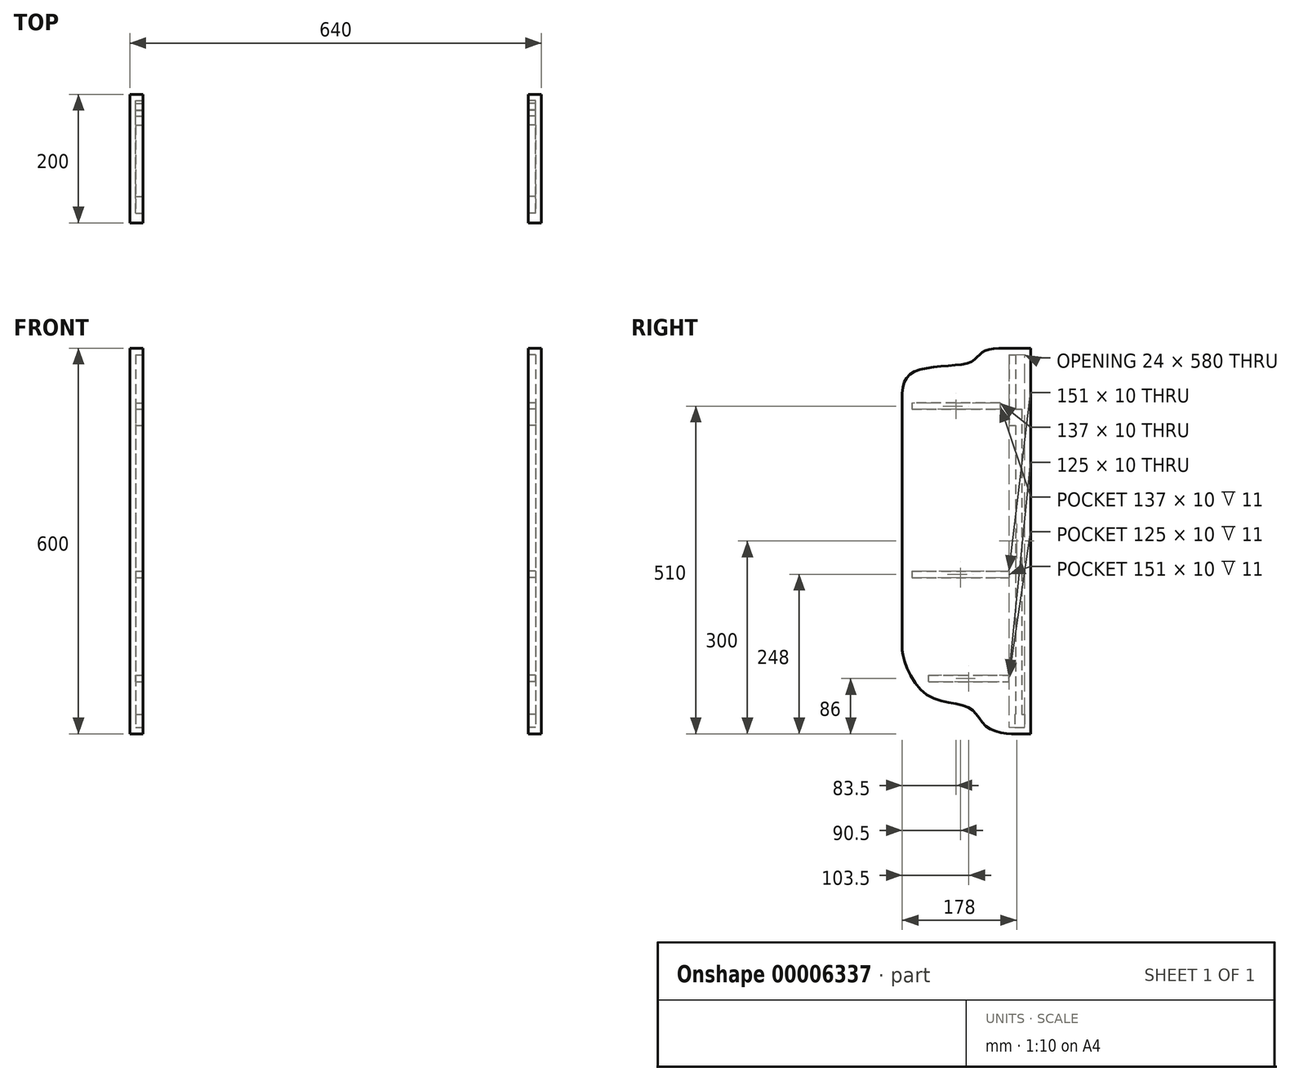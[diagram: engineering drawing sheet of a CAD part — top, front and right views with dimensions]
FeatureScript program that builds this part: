
annotation { "Feature Type Name" : "Feature", "Feature Type Description" : "" }
export const myFeature = defineFeature(function(context is Context, id is Id, definition is map)
    precondition{}
    {
        {
            var Q0;
            Q0=qCreatedBy(makeId("Right.planeOp"),FACE);
            var sketch = newSketch(context, id + "F0", { "sketchPlane" : qUnion([Q0])});
            skFitSpline(sketch, "E0.1.MirrorCS", {"points": [v(-200, 130) * mm, v(-165, 63) * mm, v(-95, 40) * mm, v(-70, 12) * mm, v(-30, 0) * mm], "startDerivative": vector(0, -133.97) * mm, "endDerivative": vector(166.38, 0) * mm});
            skLineSegment(sketch, "E0.4.MirrorCS", {"start": v(-200, 530) * mm, "end": v(-200, 117) * mm});
            skLineSegment(sketch, "E0.5.MirrorCS", {"start": v(0, 0) * mm, "end": v(0, 600) * mm});
            skLineSegment(sketch, "E1", {"start": v(-30, 0) * mm, "end": v(0, 0) * mm});
            skLineSegment(sketch, "E2.7", {"start": v(-40, 600) * mm, "end": v(0, 600) * mm});
            skFitSpline(sketch, "E3", {"points": [v(-1.8, 598.78) * mm, v(-75, 594) * mm, v(-95, 578) * mm, v(-180, 564) * mm, v(-198.07, 512.13) * mm], "startDerivative": vector(-411.19, 17.95) * mm, "endDerivative": vector(63.67, -327.47) * mm});
            skSolve(sketch);
        }
        {
            var Q0;
            Q0 = qSketchRegion(id + "F0", true);
            extrude(context, id + "F1", {"entities" : qUnion([Q0]), "oppositeDirection" : true, "depth" : 20 * mm});
        }
        {
            var Q0;
            Q0=qCreatedBy(makeId("Right.planeOp"),FACE);
            var sketch = newSketch(context, id + "F2", { "sketchPlane" : qUnion([Q0])});
            skLineSegment(sketch, "E4.13", {"start": v(-14, 495) * mm, "end": v(0, 495) * mm});
            skLineSegment(sketch, "E4.11", {"start": v(-20, 520) * mm, "end": v(0, 520) * mm});
            skLineSegment(sketch, "E4.14", {"start": v(-14, 505) * mm, "end": v(-14, 495) * mm});
            skLineSegment(sketch, "E4.16", {"start": v(-24, 505) * mm, "end": v(-24, 455) * mm});
            skLineSegment(sketch, "E4.10", {"start": v(-20, 520) * mm, "end": v(-20, 570) * mm});
            skLineSegment(sketch, "E4.17", {"start": v(-38, 455) * mm, "end": v(-24, 455) * mm});
            skLineSegment(sketch, "E4.9", {"start": v(-20, 570) * mm, "end": v(0, 570) * mm});
            skLineSegment(sketch, "E4.1", {"start": v(-38, 593.5) * mm, "end": v(-38, 455) * mm});
            skLineSegment(sketch, "E4.15", {"start": v(-14, 505) * mm, "end": v(-24, 505) * mm});
            skLineSegment(sketch, "E5", {"start": v(-36.5, 593.5) * mm, "end": v(-36.5, 594.5) * mm});
            skLineSegment(sketch, "E6", {"start": v(-32.5, 598.5) * mm, "end": v(-29.5, 598.5) * mm});
            skLineSegment(sketch, "E7", {"start": v(-38, 593.5) * mm, "end": v(-36.5, 593.5) * mm});
            skLineSegment(sketch, "E4.6", {"start": v(-29.5, 598.5) * mm, "end": v(-29.5, 600) * mm});
            skLineSegment(sketch, "E8.0", {"start": v(-29.5, 600) * mm, "end": v(0, 600) * mm});
            skPoint(sketch, "E9.orphan", {"position": v(-40, 600) * mm});
            skLineSegment(sketch, "E10.0", {"start": v(0, 495) * mm, "end": v(0, 520) * mm});
            skLineSegment(sketch, "E11.trimOffspring", {"start": v(0, 570) * mm, "end": v(0, 600) * mm});
            skPoint(sketch, "E12.orphan", {"position": v(0, 0) * mm});
            skLineSegment(sketch, "E13", {"start": v(-24, 463.64) * mm, "end": v(-24, 11.38) * mm, "construction": true});
            skLineSegment(sketch, "E14.bottom", {"start": v(0, 40) * mm, "end": v(-14, 40) * mm});
            skLineSegment(sketch, "E14.top", {"start": v(0, 0) * mm, "end": v(-30, 0) * mm});
            skLineSegment(sketch, "E14.left", {"start": v(0, 40) * mm, "end": v(0, 0) * mm});
            skLineSegment(sketch, "E14.right", {"start": v(-30, 40) * mm, "end": v(-30, 0) * mm});
            skLineSegment(sketch, "E15.top", {"start": v(-24, 30) * mm, "end": v(-14, 30) * mm});
            skLineSegment(sketch, "E15.left", {"start": v(-24, 40) * mm, "end": v(-24, 30) * mm});
            skLineSegment(sketch, "E15.right", {"start": v(-14, 40) * mm, "end": v(-14, 30) * mm});
            skLineSegment(sketch, "E16.trimOffspring", {"start": v(-24, 40) * mm, "end": v(-30, 40) * mm});
            skLineSegment(sketch, "E17.bottom", {"start": v(-190, 502) * mm, "end": v(-38, 502) * mm});
            skLineSegment(sketch, "E17.top", {"start": v(-190, 518) * mm, "end": v(-38, 518) * mm});
            skLineSegment(sketch, "E17.left", {"start": v(-190, 502) * mm, "end": v(-190, 518) * mm});
            skLineSegment(sketch, "E17.right", {"start": v(-38, 502) * mm, "end": v(-38, 518) * mm});
            skLineSegment(sketch, "E18.bottom", {"start": v(-190, 256) * mm, "end": v(-24, 256) * mm});
            skLineSegment(sketch, "E18.top", {"start": v(-190, 240) * mm, "end": v(-24, 240) * mm});
            skLineSegment(sketch, "E18.left", {"start": v(-190, 256) * mm, "end": v(-190, 240) * mm});
            skLineSegment(sketch, "E18.right", {"start": v(-24, 256) * mm, "end": v(-24, 240) * mm});
            skLineSegment(sketch, "E19.bottom", {"start": v(-164, 94) * mm, "end": v(-24, 94) * mm});
            skLineSegment(sketch, "E19.top", {"start": v(-164, 78) * mm, "end": v(-24, 78) * mm});
            skLineSegment(sketch, "E19.left", {"start": v(-164, 94) * mm, "end": v(-164, 78) * mm});
            skLineSegment(sketch, "E19.right", {"start": v(-24, 94) * mm, "end": v(-24, 78) * mm});
            skPoint(sketch, "E20.visualSharp", {"position": v(-36.5, 598.5) * mm});
            skArc(sketch, "E20.filletArc", {"start": v(-32.5, 598.5) * mm, "mid": v(-35.33, 597.33) * mm, "end": v(-36.5, 594.5) * mm});
            skSolve(sketch);
        }
        {
            var Q0;
            Q0=qCreatedBy(makeId("Right.planeOp"),FACE);
            var sketch = newSketch(context, id + "F3", { "sketchPlane" : qUnion([Q0])});
            skLineSegment(sketch, "E21", {"start": v(-48, 515) * mm, "end": v(-185, 515) * mm});
            skLineSegment(sketch, "E22.0.1.1", {"start": v(-185, 243) * mm, "end": v(-34, 243) * mm});
            skLineSegment(sketch, "E23.bottom", {"start": v(-159, 81) * mm, "end": v(-34, 81) * mm});
            skLineSegment(sketch, "E24", {"start": v(-185, 505) * mm, "end": v(-48, 505) * mm});
            skLineSegment(sketch, "E23.top", {"start": v(-159, 91) * mm, "end": v(-34, 91) * mm});
            skLineSegment(sketch, "E22.direction2", {"start": v(-185, 515) * mm, "end": v(-185, 253) * mm, "construction": true});
            skLineSegment(sketch, "E25.direction2", {"start": v(-185, 253) * mm, "end": v(-185, 91) * mm, "construction": true});
            skLineSegment(sketch, "E22.direction1", {"start": v(-185, 515) * mm, "end": v(-17.06, 515) * mm, "construction": true});
            skLineSegment(sketch, "E26", {"start": v(-34, 253) * mm, "end": v(-34, 243) * mm});
            skLineSegment(sketch, "E27", {"start": v(-48, 515) * mm, "end": v(-48, 505) * mm});
            skLineSegment(sketch, "E23.left", {"start": v(-159, 81) * mm, "end": v(-159, 91) * mm});
            skLineSegment(sketch, "E23.right", {"start": v(-34, 81) * mm, "end": v(-34, 91) * mm});
            skLineSegment(sketch, "E22.0.1.3", {"start": v(-185, 253) * mm, "end": v(-185, 243) * mm});
            skLineSegment(sketch, "E28", {"start": v(-185, 515) * mm, "end": v(-185, 505) * mm});
            skLineSegment(sketch, "E29.right", {"start": v(75.94, -256.64) * mm, "end": v(75.94, -271.64) * mm});
            skLineSegment(sketch, "E29.left", {"start": v(63.94, -256.64) * mm, "end": v(63.94, -271.64) * mm});
            skLineSegment(sketch, "E29.bottom", {"start": v(63.94, -256.64) * mm, "end": v(75.94, -256.64) * mm});
            skLineSegment(sketch, "E29.top", {"start": v(63.94, -271.64) * mm, "end": v(75.94, -271.64) * mm});
            skLineSegment(sketch, "E30", {"start": v(0, 600) * mm, "end": v(-118.45, 600) * mm, "construction": true});
            skLineSegment(sketch, "E31.0", {"start": v(-200, 530) * mm, "end": v(-200, 117) * mm, "construction": true});
            skLineSegment(sketch, "E32", {"start": v(-185, 253) * mm, "end": v(-34, 253) * mm});
            skLineSegment(sketch, "E33.bottom", {"start": v(-34, 590) * mm, "end": v(-24, 590) * mm});
            skLineSegment(sketch, "E33.top", {"start": v(-34, 480) * mm, "end": v(-24, 480) * mm});
            skLineSegment(sketch, "E33.left", {"start": v(-34, 590) * mm, "end": v(-34, 480) * mm});
            skLineSegment(sketch, "E33.right", {"start": v(-24, 590) * mm, "end": v(-24, 480) * mm});
            skLineSegment(sketch, "E34.0", {"start": v(-38, 593.5) * mm, "end": v(-38, 455) * mm, "construction": true});
            skLineSegment(sketch, "E35.0", {"start": v(-20, 520) * mm, "end": v(-20, 570) * mm, "construction": true});
            skLineSegment(sketch, "E36", {"start": v(-29, 592.32) * mm, "end": v(-29, 457.46) * mm, "construction": true});
            skLineSegment(sketch, "E37", {"start": v(-24, 471.27) * mm, "end": v(-24, -9.99) * mm, "construction": true});
            skLineSegment(sketch, "E38", {"start": v(-34, 253) * mm, "end": v(-34, 80) * mm, "construction": true});
            skLineSegment(sketch, "E39.bottom", {"start": v(-25, 30) * mm, "end": v(-10, 30) * mm});
            skLineSegment(sketch, "E39.top", {"start": v(-25, 10) * mm, "end": v(-10, 10) * mm});
            skLineSegment(sketch, "E39.left", {"start": v(-25, 30) * mm, "end": v(-25, 10) * mm});
            skLineSegment(sketch, "E39.right", {"start": v(-10, 30) * mm, "end": v(-10, 10) * mm});
            skSolve(sketch);
        }
        {
            var Q0;
            Q0 = qSketchRegion(id + "F3", true);
            extrude(context, id + "F4", {"entities" : qUnion([Q0]), "operationType" : NewBodyOperationType.REMOVE, "oppositeDirection" : true, "depth" : 11 * mm});
        }
        {
            var Q0;
            Q0=qCreatedBy(makeId("Right.planeOp"),FACE);
            var sketch = newSketch(context, id + "F5", { "sketchPlane" : qUnion([Q0])});
            skLineSegment(sketch, "E40.bottom", {"start": v(-24, 505) * mm, "end": v(-14, 505) * mm});
            skLineSegment(sketch, "E40.top", {"start": v(-24, 30) * mm, "end": v(-14, 30) * mm});
            skLineSegment(sketch, "E40.left", {"start": v(-24, 505) * mm, "end": v(-24, 30) * mm});
            skLineSegment(sketch, "E40.right", {"start": v(-14, 505) * mm, "end": v(-14, 30) * mm});
            skSolve(sketch);
        }
        {
            var Q0;
            Q0 = qSketchRegion(id + "F5", true);
            extrude(context, id + "F6", {"entities" : qUnion([Q0]), "operationType" : NewBodyOperationType.REMOVE, "oppositeDirection" : true, "depth" : 11 * mm});
        }
        {
            var Q0;
            Q0=qCreatedBy(makeId("Right.planeOp"),FACE);
            cPlane(context, id + "F7", {"entities" : qUnion([Q0]), "cplaneType" : CPlaneType.OFFSET, "offset" : 300 * mm, "width" : 150 * mm, "height" : 150 * mm});
        }
        {
            var Q0;
            Q0=makeQuery(id+"F1.opExtrude","SWEPT_BODY",BODY,{"disambiguationData":[OSD([sQuery(id+"F0.wireOp",EDGE,"E0.1.MirrorCS"),sQuery(id+"F0.wireOp",EDGE,"E0.4.MirrorCS"),sQuery(id+"F0.wireOp",EDGE,"E0.5.MirrorCS"),sQuery(id+"F0.wireOp",EDGE,"E1"),sQuery(id+"F0.wireOp",EDGE,"E2.7"),sQuery(id+"F0.wireOp",EDGE,"E3")])]});
            var Q1;
            Q1=qCreatedBy(id+"F7.planeOp",FACE);
            mirror(context, id + "F8", {"entities" : qUnion([Q0]), "mirrorPlane" : qUnion([Q1])});
        }
    });
